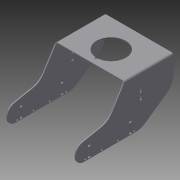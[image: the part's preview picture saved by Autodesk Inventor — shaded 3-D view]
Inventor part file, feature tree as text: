
AUTODESK INVENTOR PART (.ipt)
format: ipt  version: 2015 (Build 190159000, 159)  size: 389,632 bytes
history: native  units: mm
features: sketch x3, other x2, extrude x1
ambient origin geometry x8: Origin, YZ Plane, XZ Plane, XY Plane, X Axis, Y Axis, Z Axis, Center Point
bodies: Body1 (feature_tree)
feature tree (6):
  extrude  "Extrusion25"  Depth=3.0mm TaperAngle=0.0deg
  other  "Bend Part37"
  other  "Bend Part38"
  sketch  "Sketch44"  dims[d19=5.0mm d127=97.0mm d151=5.0mm d163=5.0mm d222=5.0mm d248=40.0mm d294=25.0mm d324=5.0mm d326=25.0mm d329=25.0mm d344=6.0mm d358=6.0mm d404=5.0mm d406=45.0mm d445=20.0mm d446=30.0mm d448=45.0deg d460=5.606189mm d463=30.0deg d467=42.0mm d468=36.0mm d469=150.0deg d483=12.0mm d486=42.0mm d487=150.0deg d488=36.0mm d489=150.0deg d528=20.0mm d530=65.0mm]
  sketch  "Sketch45"  dims[d726=80.0mm d727=50.0mm d728=200.0mm d729=100.0mm d730=70.0mm d731=180.0mm d732=20.0mm d733=100.0mm d734=50.0mm d735=50.0mm d736=25.0mm d737=5.0mm d738=5.0mm d739=150.0mm d740=5.0mm d741=5.0mm d742=30.0mm d743=10.0mm d744=6.0mm d745=97.0mm d746=73.0mm d747=4.0mm d748=8.0mm d749=8.0mm d750=7.0mm d751=4.0mm d752=8.0mm d753=8.0mm d754=1.0mm d755=8.0mm d756=4.0mm d757=7.0mm d758=8.0mm d759=4.0mm d760=8.0mm d761=30.0mm d762=8.0mm d763=1.0mm d764=30.0mm d765=8.0mm d766=4.0mm d767=8.0mm d768=4.0mm d769=30.0mm d770=7.0mm d771=5.0mm d772=8.0mm d773=4.0mm d774=8.0mm d775=4.0mm d776=30.0mm d777=7.0mm d778=5.0mm d779=90.0mm d780=97.0mm d781=6.0mm d782=10.0mm d783=73.0mm d784=65.0mm d785=100.0mm d786=200.0mm d787=5.0mm d788=2.5mm d789=50.0mm d790=2.5mm d791=5.0mm d792=5.0mm d793=50.0mm d794=5.0mm d795=5.0mm d796=50.0mm d797=5.0mm d798=5.0mm d799=50.0mm d800=5.0mm d801=5.0mm d802=50.0mm d803=10.0mm d804=6.0mm d805=10.0mm d806=10.0mm d807=10.0mm d808=6.0mm d809=3.0mm d810=0.0mm]
  sketch  "Sketch46"  dims[d811=3.0mm d812=90.0deg d813=3.0mm d814=90.0deg]
